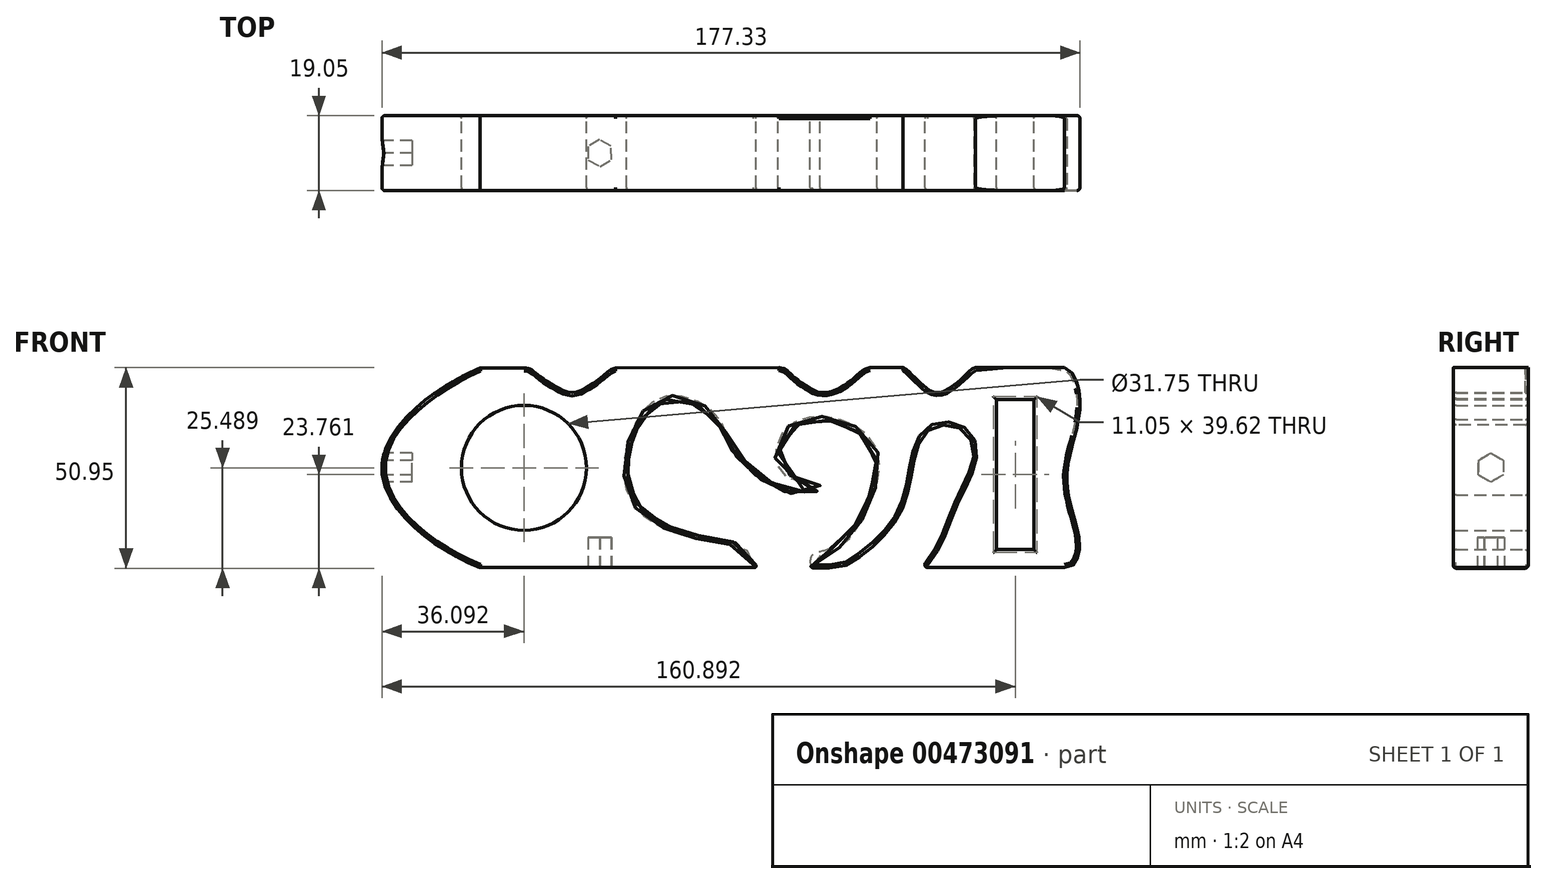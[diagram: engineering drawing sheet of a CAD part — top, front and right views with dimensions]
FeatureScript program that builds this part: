
annotation { "Feature Type Name" : "Feature", "Feature Type Description" : "" }
export const myFeature = defineFeature(function(context is Context, id is Id, definition is map)
    precondition{}
    {
        {
            var Q0;
            Q0=qCreatedBy(makeId("Front.planeOp"),FACE);
            var sketch = newSketch(context, id + "F0", { "sketchPlane" : qUnion([Q0])});
            skLineSegment(sketch, "E0.MirrorCS", {"start": v(-44.5, 42.66) * mm, "end": v(-44.5, 4.56) * mm});
            skLineSegment(sketch, "E1.MirrorCS", {"start": v(-44.5, 4.56) * mm, "end": v(-54.03, 4.56) * mm});
            skLineSegment(sketch, "E2.MirrorCS", {"start": v(-36.72, 0) * mm, "end": v(-73.16, 0) * mm});
            skLineSegment(sketch, "E3.MirrorCS", {"start": v(-44.5, 42.66) * mm, "end": v(-54.03, 42.66) * mm});
            skLineSegment(sketch, "E4.MirrorCS", {"start": v(-54.03, 42.66) * mm, "end": v(-54.03, 4.56) * mm});
            skLineSegment(sketch, "E5.MirrorCS", {"start": v(-36.72, 50.8) * mm, "end": v(-59.36, 50.8) * mm});
            skLineSegment(sketch, "E6.MirrorCS", {"start": v(-44.5, 42.63) * mm, "end": v(-54.03, 42.66) * mm});
            skLineSegment(sketch, "E7.MirrorCS", {"start": v(-44.5, 42.63) * mm, "end": v(-44.5, 4.56) * mm});
            skFitSpline(sketch, "E8", {"points": [v(-73.16, 0) * mm, v(-64.97, 15.74) * mm, v(-59.74, 29.56) * mm, v(-64.04, 35.78) * mm, v(-70.58, 35.4) * mm, v(-73.04, 32.82) * mm, v(-74.41, 29.56) * mm, v(-75.67, 23.48) * mm, v(-78.19, 14.46) * mm, v(-85.02, 5.8) * mm, v(-94.06, 0) * mm, v(-97.76, 0) * mm, v(-100.88, 0) * mm, v(-101.35, 1.25) * mm, v(-100.73, 3.27) * mm, v(-94.8, 5.5) * mm, v(-86.47, 17.78) * mm, v(-85.09, 29.8) * mm, v(-94.63, 37.08) * mm, v(-106.55, 35.22) * mm, v(-109.36, 26.86) * mm, v(-104.94, 22.83) * mm, v(-99.1, 21.65) * mm, v(-99.78, 19.23) * mm, v(-108.1, 19.4) * mm, v(-116.45, 24.55) * mm, v(-122.68, 32.05) * mm, v(-125.92, 38.45) * mm, v(-139.68, 42.23) * mm, v(-147.95, 23.8) * mm, v(-142.75, 13.4) * mm, v(-132.35, 8.7) * mm, v(-122.28, 6.75) * mm, v(-116.48, 4.6) * mm, v(-115.16, 1.38) * mm, v(-115.74, 0) * mm], "startDerivative": vector(360.55, 394.2) * mm, "endDerivative": vector(-198.38, 0) * mm});
            skCircle(sketch, "E9", {"center": v(-174.07, 25.34) * mm, "radius": 15.88 * mm});
            skFitSpline(sketch, "E10", {"points": [v(-185.25, 50.77) * mm, v(-210.16, 25.28) * mm, v(-185.25, 0) * mm], "startDerivative": vector(-82.74, -37.63) * mm, "endDerivative": vector(82.93, -34.55) * mm});
            skFitSpline(sketch, "E11.trimOffspring", {"points": [v(-73.16, 0) * mm, v(-64.97, 15.74) * mm, v(-59.74, 29.56) * mm, v(-64.04, 35.78) * mm, v(-70.58, 35.4) * mm, v(-73.04, 32.82) * mm, v(-74.41, 29.56) * mm, v(-75.67, 23.48) * mm, v(-78.19, 14.46) * mm, v(-85.02, 5.8) * mm, v(-94.06, 0) * mm, v(-97.76, 0) * mm, v(-100.88, 0) * mm, v(-101.35, 1.25) * mm, v(-100.73, 3.27) * mm, v(-94.8, 5.5) * mm, v(-86.47, 17.78) * mm, v(-85.09, 29.8) * mm, v(-94.63, 37.08) * mm, v(-106.55, 35.22) * mm, v(-109.36, 26.86) * mm, v(-104.94, 22.83) * mm, v(-99.1, 21.65) * mm, v(-99.78, 19.23) * mm, v(-108.1, 19.4) * mm, v(-116.45, 24.55) * mm, v(-122.68, 32.05) * mm, v(-125.92, 38.45) * mm, v(-139.68, 42.23) * mm, v(-147.95, 23.8) * mm, v(-142.75, 13.4) * mm, v(-132.35, 8.7) * mm, v(-122.28, 6.75) * mm, v(-116.48, 4.6) * mm, v(-115.16, 1.38) * mm, v(-115.74, 0) * mm], "startDerivative": vector(360.55, 394.2) * mm, "endDerivative": vector(-198.38, 0) * mm});
            skLineSegment(sketch, "E12.trimOffspring", {"start": v(-94.06, 0) * mm, "end": v(-94.06, 0) * mm});
            skLineSegment(sketch, "E13.trimOffspring", {"start": v(-115.74, 0) * mm, "end": v(-166.2, 0) * mm});
            skLineSegment(sketch, "E14.trimOffspring", {"start": v(-115.74, 0) * mm, "end": v(-185.25, 0) * mm});
            skFitSpline(sketch, "E15", {"points": [v(-174.06, 50.77) * mm, v(-170.59, 49.03) * mm, v(-166.33, 46.17) * mm, v(-161.76, 44.43) * mm, v(-157.92, 45.93) * mm, v(-154.27, 48.49) * mm, v(-150.84, 50.78) * mm], "startDerivative": vector(31.55, 0) * mm, "endDerivative": vector(16.63, 0) * mm});
            skFitSpline(sketch, "E16", {"points": [v(-109.3, 50.79) * mm, v(-106.08, 48.93) * mm, v(-102.53, 46.27) * mm, v(-98.08, 44.44) * mm, v(-93.09, 46.05) * mm, v(-89.75, 48.6) * mm, v(-86.09, 50.8) * mm], "startDerivative": vector(32.76, 0.26) * mm, "endDerivative": vector(25.22, -0.17) * mm});
            skFitSpline(sketch, "E17", {"points": [v(-77.88, 50.8) * mm, v(-76.48, 49.99) * mm, v(-73.85, 47.4) * mm, v(-68.96, 44.44) * mm, v(-64.08, 46.99) * mm, v(-62.05, 48.79) * mm, v(-59.27, 50.8) * mm], "startDerivative": vector(15.46, 0) * mm, "endDerivative": vector(15.93, 0) * mm});
            skLineSegment(sketch, "E18.trimOffspring", {"start": v(-174.06, 50.77) * mm, "end": v(-185.25, 50.77) * mm});
            skLineSegment(sketch, "E19.trimOffspring", {"start": v(-109.24, 50.79) * mm, "end": v(-150.84, 50.78) * mm});
            skLineSegment(sketch, "E20.trimOffspring", {"start": v(-77.74, 50.8) * mm, "end": v(-86.12, 50.8) * mm});
            skPoint(sketch, "E21.3.internal.snap0", {"position": v(-44.5, 23.6) * mm});
            skFitSpline(sketch, "E21", {"points": [v(-36.72, 50.8) * mm, v(-33.73, 47.34) * mm, v(-33.23, 37.37) * mm, v(-36.19, 23.6) * mm, v(-33.97, 11.42) * mm, v(-33.11, 3.8) * mm, v(-36.72, 0) * mm], "startDerivative": vector(31.63, -6.4) * mm, "endDerivative": vector(-51.17, 0) * mm});
            skSolve(sketch);
        }
        {
            var Q0;
            Q0=makeQuery(id+"F0.imprint","IMPRINT",FACE,{"disambiguationData":[TD([[makeQuery(id+"F0.imprint","IMPRINT",EDGE,{"derivedFrom":sQuery(id+"F0.wireOp",EDGE,"E0.MirrorCS")}),1.0]])]});
            extrude(context, id + "F1", {"entities" : qUnion([Q0]), "depth" : 19.05 * mm});
        }
        {
            var Q0;
            Q0=makeQuery(id+"F1.opExtrude","CAP_EDGE",EDGE,{"disambiguationData":[OSD([sQuery(id+"F0.wireOp",EDGE,"E8"),sQuery(id+"F0.wireOp",EDGE,"E11.trimOffspring")])],"isStart":false});
            var Q1;
            Q1=makeQuery(id+"F1.opExtrude","CAP_EDGE",EDGE,{"disambiguationData":[OSD([sQuery(id+"F0.wireOp",EDGE,"E10")])],"isStart":false});
            var Q2;
            Q2=makeQuery(id+"F1.opExtrude","CAP_EDGE",EDGE,{"disambiguationData":[OSD([sQuery(id+"F0.wireOp",EDGE,"E10")])],"isStart":true});
            var Q3;
            Q3=makeQuery(id+"F1.opExtrude","CAP_EDGE",EDGE,{"disambiguationData":[OSD([sQuery(id+"F0.wireOp",EDGE,"E18.trimOffspring")])],"isStart":true});
            var Q4;
            Q4=makeQuery(id+"F1.opExtrude","CAP_EDGE",EDGE,{"disambiguationData":[OSD([sQuery(id+"F0.wireOp",EDGE,"E18.trimOffspring")])],"isStart":false});
            var Q5;
            Q5=makeQuery(id+"F1.opExtrude","CAP_EDGE",EDGE,{"disambiguationData":[OSD([sQuery(id+"F0.wireOp",EDGE,"E16")])],"isStart":true});
            var Q6;
            Q6=makeQuery(id+"F1.opExtrude","CAP_EDGE",EDGE,{"disambiguationData":[OSD([sQuery(id+"F0.wireOp",EDGE,"E16")])],"isStart":false});
            var Q7;
            Q7=makeQuery(id+"F1.opExtrude","CAP_EDGE",EDGE,{"disambiguationData":[OSD([sQuery(id+"F0.wireOp",EDGE,"E17")])],"isStart":true});
            var Q8;
            Q8=makeQuery(id+"F1.opExtrude","CAP_EDGE",EDGE,{"disambiguationData":[OSD([sQuery(id+"F0.wireOp",EDGE,"E17")])],"isStart":false});
            var Q9;
            Q9=makeQuery(id+"F1.opExtrude","CAP_EDGE",EDGE,{"disambiguationData":[OSD([sQuery(id+"F0.wireOp",EDGE,"E21")])],"isStart":false});
            var Q10;
            Q10=makeQuery(id+"F1.opExtrude","CAP_EDGE",EDGE,{"disambiguationData":[OSD([sQuery(id+"F0.wireOp",EDGE,"E21")])],"isStart":true});
            fillet(context, id + "F2", {"entities" : qUnion([Q0, Q1, Q2, Q3, Q4, Q5, Q6, Q7, Q8, Q9, Q10]), "radius" : 0.76 * mm, "tangentPropagation" : true, "allowEdgeOverflow" : false});
        }
        {
            var Q0;
            Q0=makeQuery(id+"F1.opExtrude","CAP_EDGE",EDGE,{"disambiguationData":[OSD([sQuery(id+"F0.wireOp",EDGE,"E8"),sQuery(id+"F0.wireOp",EDGE,"E11.trimOffspring")])],"isStart":true});
            var Q1;
            Q1=makeQuery(id+"F1.opExtrude","CAP_EDGE",EDGE,{"disambiguationData":[OSD([sQuery(id+"F0.wireOp",EDGE,"E9")])],"isStart":true});
            var Q2;
            Q2=makeQuery(id+"F1.opExtrude","CAP_EDGE",EDGE,{"disambiguationData":[OSD([sQuery(id+"F0.wireOp",EDGE,"E9")])],"isStart":false});
            var Q3;
            Q3=makeQuery(id+"F1.opExtrude","CAP_EDGE",EDGE,{"disambiguationData":[OSD([sQuery(id+"F0.wireOp",EDGE,"E3.MirrorCS")])],"isStart":true});
            var Q4;
            Q4=makeQuery(id+"F1.opExtrude","CAP_EDGE",EDGE,{"disambiguationData":[OSD([sQuery(id+"F0.wireOp",EDGE,"E4.MirrorCS")])],"isStart":true});
            var Q5;
            Q5=makeQuery(id+"F1.opExtrude","CAP_EDGE",EDGE,{"disambiguationData":[OSD([sQuery(id+"F0.wireOp",EDGE,"E0.MirrorCS"),sQuery(id+"F0.wireOp",EDGE,"E7.MirrorCS")])],"isStart":true});
            var Q6;
            Q6=makeQuery(id+"F1.opExtrude","CAP_EDGE",EDGE,{"disambiguationData":[OSD([sQuery(id+"F0.wireOp",EDGE,"E1.MirrorCS")])],"isStart":true});
            var Q7;
            Q7=makeQuery(id+"F1.opExtrude","CAP_EDGE",EDGE,{"disambiguationData":[OSD([sQuery(id+"F0.wireOp",EDGE,"E0.MirrorCS"),sQuery(id+"F0.wireOp",EDGE,"E7.MirrorCS")])],"isStart":false});
            var Q8;
            Q8=makeQuery(id+"F1.opExtrude","CAP_EDGE",EDGE,{"disambiguationData":[OSD([sQuery(id+"F0.wireOp",EDGE,"E4.MirrorCS")])],"isStart":false});
            var Q9;
            Q9=makeQuery(id+"F1.opExtrude","CAP_EDGE",EDGE,{"disambiguationData":[OSD([sQuery(id+"F0.wireOp",EDGE,"E3.MirrorCS")])],"isStart":false});
            var Q10;
            Q10=makeQuery(id+"F1.opExtrude","CAP_EDGE",EDGE,{"disambiguationData":[OSD([sQuery(id+"F0.wireOp",EDGE,"E1.MirrorCS")])],"isStart":false});
            fillet(context, id + "F3", {"entities" : qUnion([Q0, Q1, Q2, Q3, Q4, Q5, Q6, Q7, Q8, Q9, Q10]), "radius" : 0.76 * mm, "tangentPropagation" : true, "allowEdgeOverflow" : false});
        }
        {
            var Q0;
            Q0=makeQuery(id+"F1.opExtrude","SWEPT_FACE",FACE,{"disambiguationData":[OSD([sQuery(id+"F0.wireOp",EDGE,"E14.trimOffspring")])]});
            var sketch = newSketch(context, id + "F4", { "sketchPlane" : qUnion([Q0])});
            skCircle(sketch, "E22.cCircle", {"center": v(-154.84, 9.53) * mm, "radius": 3.4 * mm, "construction": true});
            skPoint(sketch, "E22.cCircle.centerSnap0", {"position": v(-115.74, 9.53) * mm});
            skLineSegment(sketch, "E22.0", {"start": v(-151.91, 7.79) * mm, "end": v(-154.88, 6.12) * mm});
            skLineSegment(sketch, "E22.1", {"start": v(-154.88, 6.12) * mm, "end": v(-157.8, 7.86) * mm});
            skLineSegment(sketch, "E22.2", {"start": v(-157.8, 7.86) * mm, "end": v(-157.76, 11.26) * mm});
            skLineSegment(sketch, "E22.3", {"start": v(-157.76, 11.26) * mm, "end": v(-154.8, 12.93) * mm});
            skLineSegment(sketch, "E22.4", {"start": v(-154.8, 12.93) * mm, "end": v(-151.87, 11.19) * mm});
            skLineSegment(sketch, "E22.5", {"start": v(-151.87, 11.19) * mm, "end": v(-151.91, 7.79) * mm});
            skSolve(sketch);
        }
        {
            var Q0;
            Q0=makeQuery(id+"F4.imprint","IMPRINT",FACE,{"disambiguationData":[TD([[makeQuery(id+"F4.imprint","IMPRINT",EDGE,{"derivedFrom":sQuery(id+"F4.wireOp",EDGE,"E22.0")}),-1.0]])]});
            extrude(context, id + "F5", {"entities" : qUnion([Q0]), "operationType" : NewBodyOperationType.REMOVE, "oppositeDirection" : true, "depth" : 7.62 * mm});
        }
        {
            var Q0;
            Q0=qCreatedBy(makeId("Right.planeOp"),FACE);
            cPlane(context, id + "F6", {"entities" : qUnion([Q0]), "cplaneType" : CPlaneType.OFFSET, "offset" : 210.2 * mm, "oppositeDirection" : true, "width" : 152.4 * mm, "height" : 152.4 * mm});
        }
        {
            var Q0;
            Q0=qCreatedBy(id+"F6.planeOp",FACE);
            var sketch = newSketch(context, id + "F7", { "sketchPlane" : qUnion([Q0])});
            skPoint(sketch, "E23", {"position": v(-9.52, 25.42) * mm});
            skCircle(sketch, "E24.cCircle", {"center": v(-9.52, 25.42) * mm, "radius": 3.18 * mm, "construction": true});
            skLineSegment(sketch, "E24.0", {"start": v(-12.7, 23.58) * mm, "end": v(-12.7, 27.25) * mm});
            skLineSegment(sketch, "E24.1", {"start": v(-12.7, 27.25) * mm, "end": v(-9.52, 29.08) * mm});
            skLineSegment(sketch, "E24.2", {"start": v(-9.52, 29.08) * mm, "end": v(-6.35, 27.25) * mm});
            skLineSegment(sketch, "E24.3", {"start": v(-6.35, 27.25) * mm, "end": v(-6.35, 23.58) * mm});
            skLineSegment(sketch, "E24.4", {"start": v(-6.35, 23.58) * mm, "end": v(-9.52, 21.75) * mm});
            skLineSegment(sketch, "E24.5", {"start": v(-9.52, 21.75) * mm, "end": v(-12.7, 23.58) * mm});
            skPoint(sketch, "E24.0.midPoint", {"position": v(-12.7, 25.42) * mm});
            skSolve(sketch);
        }
        {
            var Q0;
            Q0=makeQuery(id+"F7.imprint","IMPRINT",FACE,{"disambiguationData":[TD([[makeQuery(id+"F7.imprint","IMPRINT",EDGE,{"derivedFrom":sQuery(id+"F7.wireOp",EDGE,"E24.0")}),-1.0]])]});
            extrude(context, id + "F8", {"entities" : qUnion([Q0]), "operationType" : NewBodyOperationType.REMOVE, "depth" : 7.62 * mm});
        }
    });
